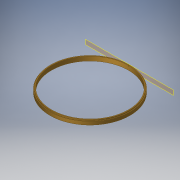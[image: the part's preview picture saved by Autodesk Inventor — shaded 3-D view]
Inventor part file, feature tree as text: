
AUTODESK INVENTOR PART (.ipt)
format: ipt  version: 2018 (Build 220112000, 112)  size: 151,040 bytes
history: native  units: in
note: dims shown in document units (in); Inventor stores cm internally (conversion verified against a paired STEP export)
features: sketch x3, extrude x2, plane x1, hole x1, pattern_circular x1
ambient origin geometry x8: Origin, YZ Plane, XZ Plane, XY Plane, X Axis, Y Axis, Z Axis, Center Point
bodies: Solid1 (feature_tree)
feature tree (8):
  extrude  "Extrusion1"  Depth=0.16in
  extrude  "Extrusion2"  Depth=0.095in
  plane  "Work Plane1"
  hole  "Hole1"  [1 undecoded]
  pattern_circular  "Circular Pattern1"  Count=6 Angle=360.0deg
  sketch  "Sketch1"  dims[d0=7.75in d1=0.16in]
  sketch  "Sketch2"  dims[d2=0.325in d3=0.0in d4=0.095in]
  sketch  "Sketch3"  dims[d5=0.095in d6=0.0in d7=0.05in d8=0.062in d9=0.157in d10=0.375in d11=0.25in d12=0.5635in d13=0.248in d14=0.8108in d15=2.3622in d16=360.0deg]
note: 1 required parameter value undecoded (feature->parameter linkage not recoverable at this tier; creation-order binding heuristic only, values carry confidence <= 0.55)
